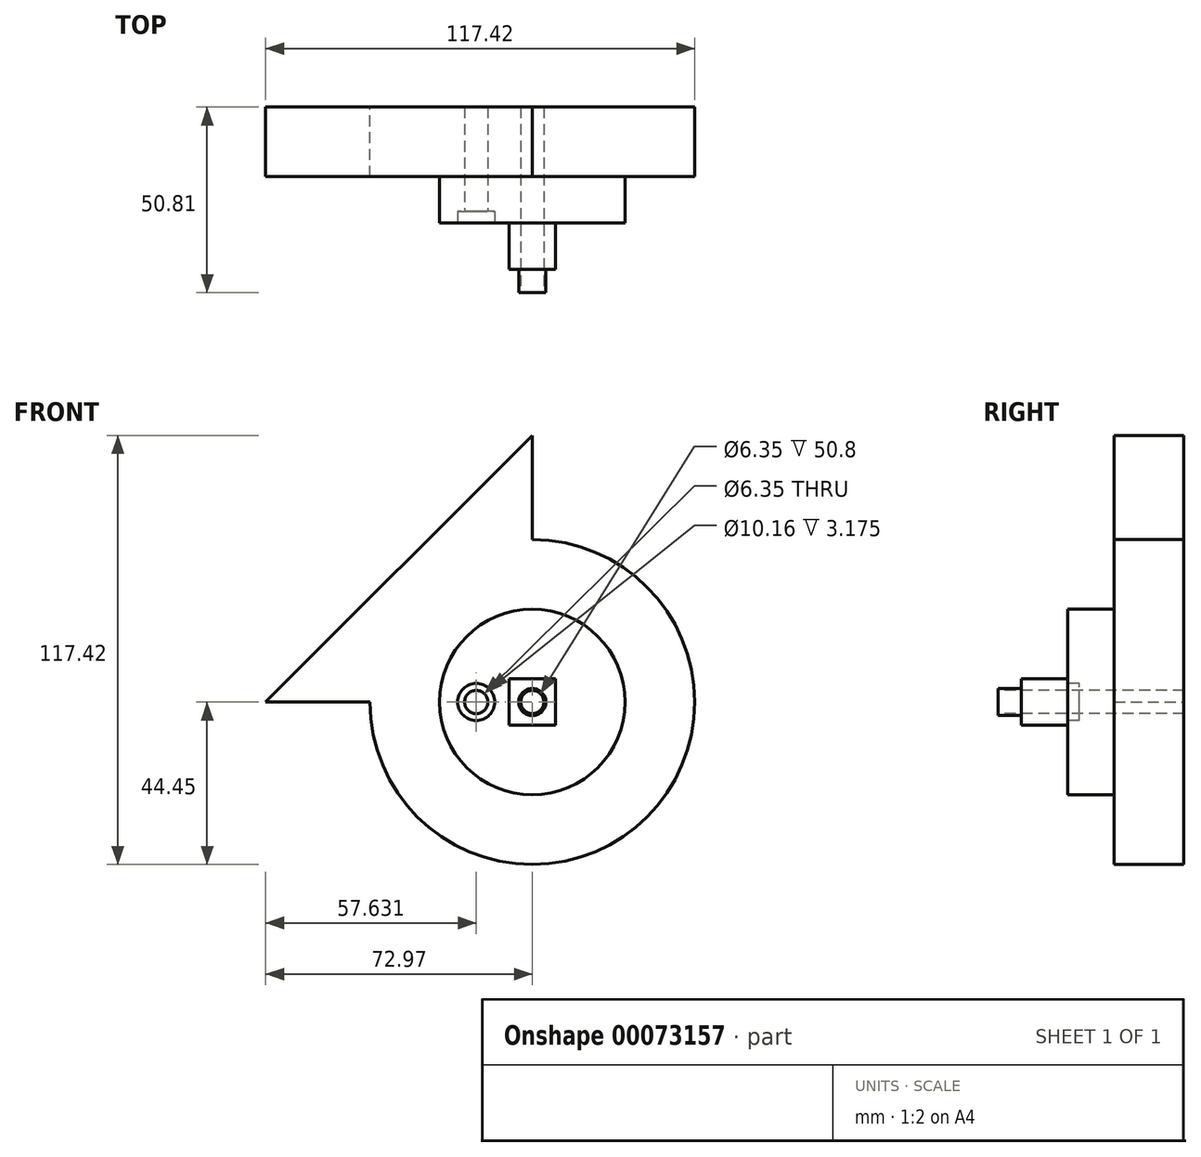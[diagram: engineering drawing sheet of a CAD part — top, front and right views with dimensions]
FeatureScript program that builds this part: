
annotation { "Feature Type Name" : "Feature", "Feature Type Description" : "" }
export const myFeature = defineFeature(function(context is Context, id is Id, definition is map)
    precondition{}
    {
        {
            var Q0;
            Q0=qCreatedBy(makeId("Front.planeOp"),FACE);
            var sketch = newSketch(context, id + "F0", { "sketchPlane" : qUnion([Q0])});
            skArc(sketch, "E0", {"start": v(-44.45, 0) * mm, "mid": v(31.43, -31.43) * mm, "end": v(0, 44.45) * mm});
            skLineSegment(sketch, "E1", {"start": v(0, 44.45) * mm, "end": v(0, 72.97) * mm});
            skLineSegment(sketch, "E2", {"start": v(0, 72.97) * mm, "end": v(-72.97, 0) * mm});
            skLineSegment(sketch, "E3", {"start": v(-72.97, 0) * mm, "end": v(-44.45, 0) * mm});
            skLineSegment(sketch, "E4", {"start": v(0, 0) * mm, "end": v(-36.49, 36.49) * mm, "construction": true});
            skSolve(sketch);
        }
        {
            var Q0;
            Q0 = qSketchRegion(id + "F0", true);
            extrude(context, id + "F1", {"entities" : qUnion([Q0]), "endBound" : BoundingType.SYMMETRIC, "depth" : 19.05 * mm});
        }
        {
            var Q0;
            Q0=makeQuery(id+"F1.opExtrude","CAP_FACE",FACE,{"disambiguationData":[OSD([sQuery(id+"F0.wireOp",EDGE,"E0"),sQuery(id+"F0.wireOp",EDGE,"E1"),sQuery(id+"F0.wireOp",EDGE,"E2"),sQuery(id+"F0.wireOp",EDGE,"E3")])],"isStart":false});
            var sketch = newSketch(context, id + "F2", { "sketchPlane" : qUnion([Q0])});
            skCircle(sketch, "E5", {"center": v(0, 0) * mm, "radius": 25.4 * mm});
            skSolve(sketch);
        }
        {
            var Q0;
            Q0 = qSketchRegion(id + "F2", true);
            extrude(context, id + "F3", {"entities" : qUnion([Q0]), "operationType" : NewBodyOperationType.ADD, "depth" : 12.7 * mm});
        }
        {
            var Q0;
            Q0=makeQuery(id+"F3.opExtrude","CAP_FACE",FACE,{"disambiguationData":[OSD([sQuery(id+"F2.wireOp",EDGE,"E5")])],"isStart":false});
            var sketch = newSketch(context, id + "F4", { "sketchPlane" : qUnion([Q0])});
            skLineSegment(sketch, "E6.rect.bottom", {"start": v(6.35, 6.35) * mm, "end": v(-6.35, 6.35) * mm});
            skLineSegment(sketch, "E6.rect.top", {"start": v(6.35, -6.35) * mm, "end": v(-6.35, -6.35) * mm});
            skLineSegment(sketch, "E6.rect.left", {"start": v(6.35, 6.35) * mm, "end": v(6.35, -6.35) * mm});
            skLineSegment(sketch, "E6.rect.right", {"start": v(-6.35, 6.35) * mm, "end": v(-6.35, -6.35) * mm});
            skPoint(sketch, "E6.rect.middle", {"position": v(0, 0) * mm});
            skSolve(sketch);
        }
        {
            var Q0;
            Q0 = qSketchRegion(id + "F4", true);
            extrude(context, id + "F5", {"entities" : qUnion([Q0]), "operationType" : NewBodyOperationType.ADD, "depth" : 12.7 * mm});
        }
        {
            var Q0;
            Q0=makeQuery(id+"F5.opExtrude","CAP_FACE",FACE,{"disambiguationData":[OSD([sQuery(id+"F4.wireOp",EDGE,"E6.rect.bottom"),sQuery(id+"F4.wireOp",EDGE,"E6.rect.top"),sQuery(id+"F4.wireOp",EDGE,"E6.rect.left"),sQuery(id+"F4.wireOp",EDGE,"E6.rect.right")])],"isStart":false});
            var sketch = newSketch(context, id + "F6", { "sketchPlane" : qUnion([Q0])});
            skCircle(sketch, "E7", {"center": v(0, 0) * mm, "radius": 3.7 * mm});
            skSolve(sketch);
        }
        {
            var Q0;
            Q0 = qSketchRegion(id + "F6", true);
            extrude(context, id + "F7", {"entities" : qUnion([Q0]), "operationType" : NewBodyOperationType.ADD, "depth" : 6.35 * mm});
        }
        {
            var Q0;
            Q0=makeQuery(id+"F7.opExtrude","CAP_FACE",FACE,{"disambiguationData":[OSD([sQuery(id+"F6.wireOp",EDGE,"E7")])],"isStart":false});
            var sketch = newSketch(context, id + "F8", { "sketchPlane" : qUnion([Q0])});
            skCircle(sketch, "E8", {"center": v(0, 0) * mm, "radius": 3.18 * mm});
            skSolve(sketch);
        }
        {
            var Q0;
            Q0=sQuery(id+"F8.wireOp",VERTEX,"E8.center");
            var Q1;
            Q1=makeQuery(id+"F1.opExtrude","SWEPT_BODY",BODY,{"disambiguationData":[OSD([sQuery(id+"F0.wireOp",EDGE,"E0"),sQuery(id+"F0.wireOp",EDGE,"E1"),sQuery(id+"F0.wireOp",EDGE,"E2"),sQuery(id+"F0.wireOp",EDGE,"E3")])]});
            hole(context, id + "F9", {"style" : HoleStyle.SIMPLE, "holeDiameter" : 6.35 * mm, "endStyle" : HoleEndStyle.THROUGH, "locations" : qUnion([Q0]), "scope" : qUnion([Q1])});
        }
        {
            var Q0;
            Q0=makeQuery(id+"F3.opExtrude","CAP_FACE",FACE,{"disambiguationData":[OSD([sQuery(id+"F2.wireOp",EDGE,"E5")])],"isStart":false});
            var sketch = newSketch(context, id + "F10", { "sketchPlane" : qUnion([Q0])});
            skCircle(sketch, "E9", {"center": v(-15.34, 0) * mm, "radius": 3.18 * mm});
            skPoint(sketch, "E9.centerSnap0", {"position": v(-6.35, 0) * mm});
            skSolve(sketch);
        }
        {
            var Q0;
            Q0=sQuery(id+"F10.wireOp",VERTEX,"E9.center");
            var Q1;
            Q1=makeQuery(id+"F1.opExtrude","SWEPT_BODY",BODY,{"disambiguationData":[OSD([sQuery(id+"F0.wireOp",EDGE,"E0"),sQuery(id+"F0.wireOp",EDGE,"E1"),sQuery(id+"F0.wireOp",EDGE,"E2"),sQuery(id+"F0.wireOp",EDGE,"E3")])]});
            hole(context, id + "F11", {"style" : HoleStyle.C_BORE, "holeDiameter" : 6.35 * mm, "cBoreDiameter" : 10.16 * mm, "cBoreDepth" : 3.17 * mm, "endStyle" : HoleEndStyle.THROUGH, "locations" : qUnion([Q0]), "scope" : qUnion([Q1])});
        }
    });
